# Revit family: GRAS_HW-25NW-K-20-30 (W)
name_source: partatom
category: Osprzęt hydrauliczny
revit_build: Autodesk Revit 2018 (Build: 20190510_1515(x64)
units: mm (PartAtom-declared; Revit-internal decimal feet)

## family parameters
Obiekt nadrzędny = Powierzchnia
Punkt obliczania pomieszczeń = Nie
Tnij formami wycięć po wczytaniu = Nie
Typ części = Normalny
Współdzielony = Nie
Wymiar okrągłego złącza = Użyj średnicy

## types (2) — shared parameters
Cabinet_Depth = 180 mm  [stored 0.590551 ft]
Cabinet_Height = 780 mm  [stored 2.55906 ft]
Cabinet_Width = 780 mm  [stored 2.55906 ft]
Cabinet_all_width = 1010 mm  [stored 3.31365 ft]
Cabinet_g_width = 230 mm  [stored 0.754593 ft]
D1 = 80 mm  [stored 0.262467 ft]
DN = 25 mm  [stored 0.082021 ft]
Flow = 60.0 L/s
H1 = 70 mm  [stored 0.229659 ft]
Hole_Depth = 190 mm  [stored 0.62336 ft]
Hole_Height = 800 mm  [stored 2.62467 ft]
Hole_L = 630 mm
Hole_R = 400 mm  [stored 1.31234 ft]
Hole_Width = 1030 mm  [stored 3.37927 ft]
K_factor = 42
Model = HW-25NW-K-20/30 W, RAL3000
Producent = GRAS PPPH
URL = http://gras.pl
W1 = 70 mm  [stored 0.229659 ft]
W2 = 40 mm  [stored 0.131234 ft]
picH = 60 mm  [stored 0.19685 ft]
zero-valued in all types: Domyślna rzędna, mounting_plane, zer0

## per-type parameters (varying)
| type | Cabinet_Material |
| HW-25NW-K-20/30 W, RAL9010 | DC01, RAL9010 |
| HW-25NW-K-20/30 W, RAL3000 | DC01, RAL3000 |

note: [stored X ft] marks values corroborated as IEEE doubles in the binary element streams (Revit-internal decimal feet)

## geometry (parser evidence)
native form markers: Blend x4
no freeform markers — native parametric forms only
